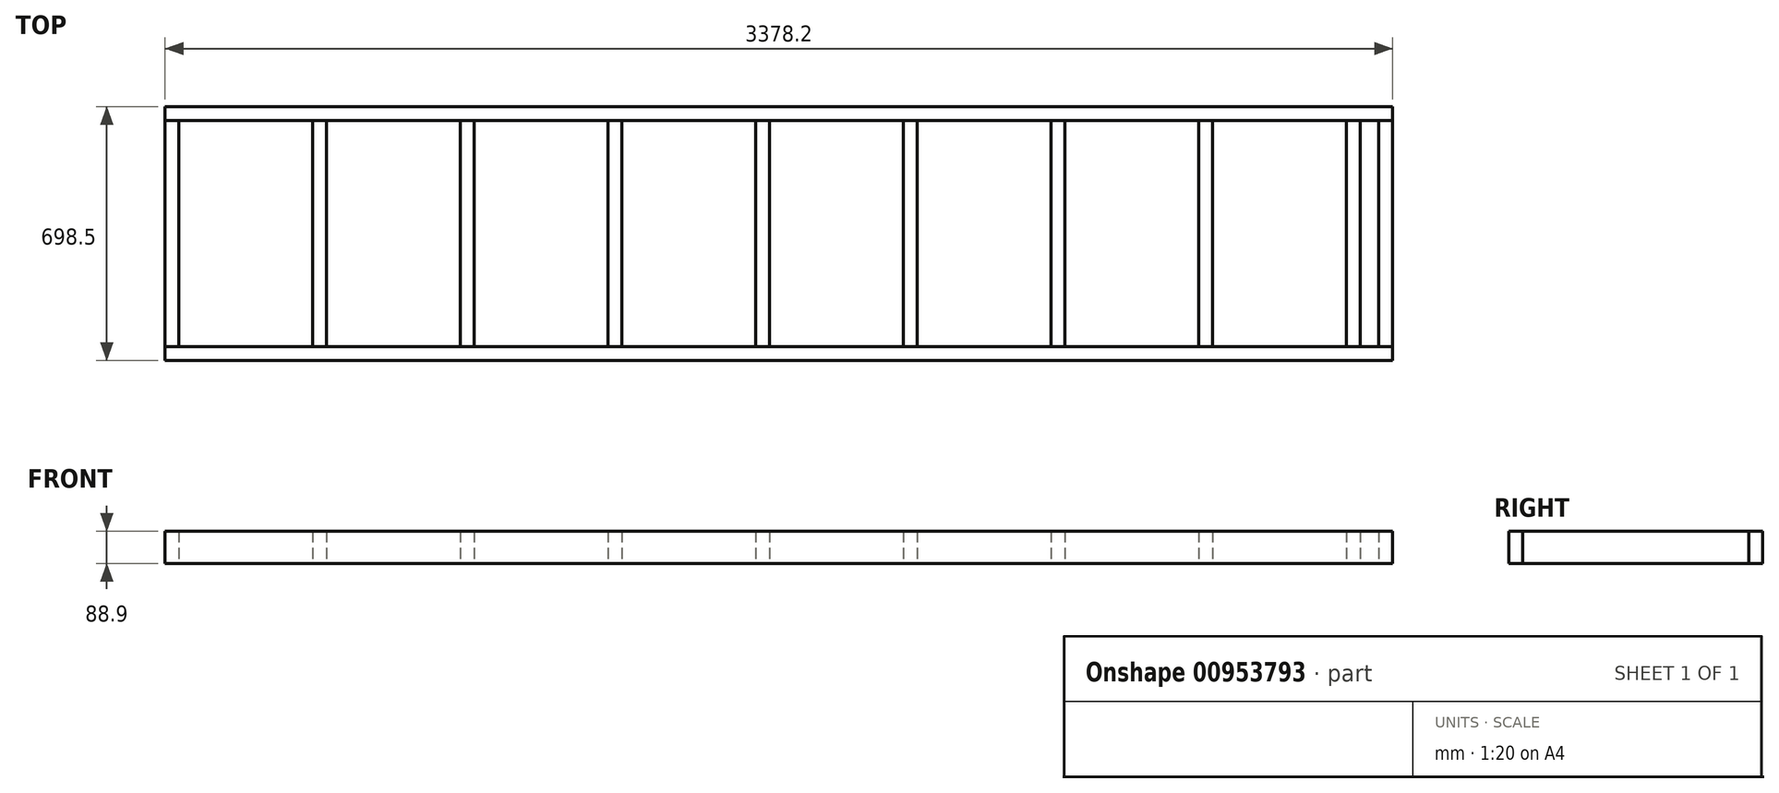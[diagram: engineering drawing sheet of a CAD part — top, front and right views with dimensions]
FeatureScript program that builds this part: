
annotation { "Feature Type Name" : "Feature", "Feature Type Description" : "" }
export const myFeature = defineFeature(function(context is Context, id is Id, definition is map)
    precondition{}
    {
        {
            var Q0;
            Q0=qCreatedBy(makeId("Top.planeOp"),FACE);
            var sketch = newSketch(context, id + "F0", { "sketchPlane" : qUnion([Q0])});
            skLineSegment(sketch, "E0.bottom", {"start": v(0, 0) * mm, "end": v(3378.2, 0) * mm});
            skLineSegment(sketch, "E0.top", {"start": v(0, 698.5) * mm, "end": v(3378.2, 698.5) * mm});
            skLineSegment(sketch, "E0.left", {"start": v(0, 0) * mm, "end": v(0, 698.5) * mm});
            skLineSegment(sketch, "E0.right", {"start": v(3378.2, 0) * mm, "end": v(3378.2, 698.5) * mm});
            skLineSegment(sketch, "E1.0", {"start": v(38.1, 38.1) * mm, "end": v(3340.1, 38.1) * mm});
            skLineSegment(sketch, "E1.1", {"start": v(38.1, 38.1) * mm, "end": v(38.1, 660.4) * mm});
            skLineSegment(sketch, "E1.2", {"start": v(38.1, 660.4) * mm, "end": v(3340.1, 660.4) * mm});
            skLineSegment(sketch, "E1.3", {"start": v(3340.1, 38.1) * mm, "end": v(3340.1, 660.4) * mm});
            skLineSegment(sketch, "E2", {"start": v(38.1, 660.4) * mm, "end": v(0, 660.4) * mm});
            skLineSegment(sketch, "E3", {"start": v(38.1, 38.1) * mm, "end": v(0, 38.1) * mm});
            skLineSegment(sketch, "E4", {"start": v(3340.1, 660.4) * mm, "end": v(3378.2, 660.4) * mm});
            skLineSegment(sketch, "E5", {"start": v(3340.1, 38.1) * mm, "end": v(3378.2, 38.1) * mm});
            skSolve(sketch);
        }
        {
            var Q0;
            {var subQ1=sQuery(id+"F0.wireOp",EDGE,"E0.top");Q0=makeQuery(id+"F0.imprint","IMPRINT",FACE,{"disambiguationData":[TD([[makeQuery(id+"F0.imprint","IMPRINT",EDGE,{"derivedFrom":subQ1}),-1.0]])]});}
            extrude(context, id + "F1", {"entities" : qUnion([Q0]), "depth" : 88.9 * mm, "offsetDistance" : 25.4 * mm});
        }
        {
            var Q0;
            {var subQ1=sQuery(id+"F0.wireOp",EDGE,"E0.bottom");Q0=makeQuery(id+"F0.imprint","IMPRINT",FACE,{"disambiguationData":[TD([[makeQuery(id+"F0.imprint","IMPRINT",EDGE,{"derivedFrom":subQ1}),1.0]])]});}
            extrude(context, id + "F2", {"entities" : qUnion([Q0]), "depth" : 88.9 * mm, "offsetDistance" : 25.4 * mm});
        }
        {
            var Q0;
            Q0=makeQuery(id+"F0.imprint","IMPRINT",FACE,{"disambiguationData":[TD([[makeQuery(id+"F0.imprint","IMPRINT",EDGE,{"derivedFrom":sQuery(id+"F0.wireOp",EDGE,"E1.1")}),1.0]])]});
            extrude(context, id + "F3", {"entities" : qUnion([Q0]), "depth" : 88.9 * mm, "offsetDistance" : 25.4 * mm});
        }
        {
            var Q0;
            Q0=makeQuery(id+"F3.opExtrude","SWEPT_BODY",BODY,{"disambiguationData":[OSD([sQuery(id+"F0.wireOp",EDGE,"E0.left"),sQuery(id+"F0.wireOp",EDGE,"E1.1"),sQuery(id+"F0.wireOp",EDGE,"E2"),sQuery(id+"F0.wireOp",EDGE,"E3")])]});
            var Q1;
            Q1=makeQuery(id+"F3.opExtrude","SWEPT_FACE",FACE,{"disambiguationData":[OSD([sQuery(id+"F0.wireOp",EDGE,"E1.1")])]});
            transform(context, id + "F4", {"entities" : qUnion([Q0]), "transformType" : TransformType.TRANSLATION_DISTANCE, "transformDirection" : qUnion([Q1]), "distance" : 406.4 * mm, "makeCopy" : true});
        }
        {
            var Q0;
            Q0=makeQuery(id+"F4.opPattern","COPY",BODY,{"derivedFrom":makeQuery(id+"F3.opExtrude","SWEPT_BODY",BODY,{"disambiguationData":[OSD([sQuery(id+"F0.wireOp",EDGE,"E0.left"),sQuery(id+"F0.wireOp",EDGE,"E1.1"),sQuery(id+"F0.wireOp",EDGE,"E2"),sQuery(id+"F0.wireOp",EDGE,"E3")])]}),"instanceName":"1"});
            var Q1;
            Q1=makeQuery(id+"F4.opPattern","COPY",FACE,{"derivedFrom":makeQuery(id+"F3.opExtrude","SWEPT_FACE",FACE,{"disambiguationData":[OSD([sQuery(id+"F0.wireOp",EDGE,"E1.1")])]}),"instanceName":"1"});
            transform(context, id + "F5", {"entities" : qUnion([Q0]), "transformType" : TransformType.TRANSLATION_DISTANCE, "transformDirection" : qUnion([Q1]), "distance" : 406.4 * mm, "makeCopy" : true});
        }
        {
            var Q0;
            Q0=makeQuery(id+"F5.opPattern","COPY",BODY,{"derivedFrom":makeQuery(id+"F4.opPattern","COPY",BODY,{"derivedFrom":makeQuery(id+"F3.opExtrude","SWEPT_BODY",BODY,{"disambiguationData":[OSD([sQuery(id+"F0.wireOp",EDGE,"E0.left"),sQuery(id+"F0.wireOp",EDGE,"E1.1"),sQuery(id+"F0.wireOp",EDGE,"E2"),sQuery(id+"F0.wireOp",EDGE,"E3")])]}),"instanceName":"1"}),"instanceName":"1"});
            var Q1;
            Q1=makeQuery(id+"F5.opPattern","COPY",FACE,{"derivedFrom":makeQuery(id+"F4.opPattern","COPY",FACE,{"derivedFrom":makeQuery(id+"F3.opExtrude","SWEPT_FACE",FACE,{"disambiguationData":[OSD([sQuery(id+"F0.wireOp",EDGE,"E1.1")])]}),"instanceName":"1"}),"instanceName":"1"});
            transform(context, id + "F6", {"entities" : qUnion([Q0]), "transformType" : TransformType.TRANSLATION_DISTANCE, "transformDirection" : qUnion([Q1]), "distance" : 406.4 * mm, "makeCopy" : true});
        }
        {
            var Q0;
            Q0=makeQuery(id+"F6.opPattern","COPY",BODY,{"derivedFrom":makeQuery(id+"F5.opPattern","COPY",BODY,{"derivedFrom":makeQuery(id+"F4.opPattern","COPY",BODY,{"derivedFrom":makeQuery(id+"F3.opExtrude","SWEPT_BODY",BODY,{"disambiguationData":[OSD([sQuery(id+"F0.wireOp",EDGE,"E0.left"),sQuery(id+"F0.wireOp",EDGE,"E1.1"),sQuery(id+"F0.wireOp",EDGE,"E2"),sQuery(id+"F0.wireOp",EDGE,"E3")])]}),"instanceName":"1"}),"instanceName":"1"}),"instanceName":"1"});
            var Q1;
            Q1=makeQuery(id+"F6.opPattern","COPY",FACE,{"derivedFrom":makeQuery(id+"F5.opPattern","COPY",FACE,{"derivedFrom":makeQuery(id+"F4.opPattern","COPY",FACE,{"derivedFrom":makeQuery(id+"F3.opExtrude","SWEPT_FACE",FACE,{"disambiguationData":[OSD([sQuery(id+"F0.wireOp",EDGE,"E1.1")])]}),"instanceName":"1"}),"instanceName":"1"}),"instanceName":"1"});
            transform(context, id + "F7", {"entities" : qUnion([Q0]), "transformType" : TransformType.TRANSLATION_DISTANCE, "transformDirection" : qUnion([Q1]), "distance" : 406.4 * mm, "makeCopy" : true});
        }
        {
            var Q0;
            Q0=makeQuery(id+"F7.opPattern","COPY",BODY,{"derivedFrom":makeQuery(id+"F6.opPattern","COPY",BODY,{"derivedFrom":makeQuery(id+"F5.opPattern","COPY",BODY,{"derivedFrom":makeQuery(id+"F4.opPattern","COPY",BODY,{"derivedFrom":makeQuery(id+"F3.opExtrude","SWEPT_BODY",BODY,{"disambiguationData":[OSD([sQuery(id+"F0.wireOp",EDGE,"E0.left"),sQuery(id+"F0.wireOp",EDGE,"E1.1"),sQuery(id+"F0.wireOp",EDGE,"E2"),sQuery(id+"F0.wireOp",EDGE,"E3")])]}),"instanceName":"1"}),"instanceName":"1"}),"instanceName":"1"}),"instanceName":"1"});
            var Q1;
            Q1=makeQuery(id+"F7.opPattern","COPY",FACE,{"derivedFrom":makeQuery(id+"F6.opPattern","COPY",FACE,{"derivedFrom":makeQuery(id+"F5.opPattern","COPY",FACE,{"derivedFrom":makeQuery(id+"F4.opPattern","COPY",FACE,{"derivedFrom":makeQuery(id+"F3.opExtrude","SWEPT_FACE",FACE,{"disambiguationData":[OSD([sQuery(id+"F0.wireOp",EDGE,"E1.1")])]}),"instanceName":"1"}),"instanceName":"1"}),"instanceName":"1"}),"instanceName":"1"});
            transform(context, id + "F8", {"entities" : qUnion([Q0]), "transformType" : TransformType.TRANSLATION_DISTANCE, "transformDirection" : qUnion([Q1]), "distance" : 406.4 * mm, "makeCopy" : true});
        }
        {
            var Q0;
            Q0=makeQuery(id+"F8.opPattern","COPY",BODY,{"derivedFrom":makeQuery(id+"F7.opPattern","COPY",BODY,{"derivedFrom":makeQuery(id+"F6.opPattern","COPY",BODY,{"derivedFrom":makeQuery(id+"F5.opPattern","COPY",BODY,{"derivedFrom":makeQuery(id+"F4.opPattern","COPY",BODY,{"derivedFrom":makeQuery(id+"F3.opExtrude","SWEPT_BODY",BODY,{"disambiguationData":[OSD([sQuery(id+"F0.wireOp",EDGE,"E0.left"),sQuery(id+"F0.wireOp",EDGE,"E1.1"),sQuery(id+"F0.wireOp",EDGE,"E2"),sQuery(id+"F0.wireOp",EDGE,"E3")])]}),"instanceName":"1"}),"instanceName":"1"}),"instanceName":"1"}),"instanceName":"1"}),"instanceName":"1"});
            var Q1;
            Q1=makeQuery(id+"F8.opPattern","COPY",FACE,{"derivedFrom":makeQuery(id+"F7.opPattern","COPY",FACE,{"derivedFrom":makeQuery(id+"F6.opPattern","COPY",FACE,{"derivedFrom":makeQuery(id+"F5.opPattern","COPY",FACE,{"derivedFrom":makeQuery(id+"F4.opPattern","COPY",FACE,{"derivedFrom":makeQuery(id+"F3.opExtrude","SWEPT_FACE",FACE,{"disambiguationData":[OSD([sQuery(id+"F0.wireOp",EDGE,"E1.1")])]}),"instanceName":"1"}),"instanceName":"1"}),"instanceName":"1"}),"instanceName":"1"}),"instanceName":"1"});
            transform(context, id + "F9", {"entities" : qUnion([Q0]), "transformType" : TransformType.TRANSLATION_DISTANCE, "transformDirection" : qUnion([Q1]), "distance" : 406.4 * mm, "makeCopy" : true});
        }
        {
            var Q0;
            Q0=makeQuery(id+"F9.opPattern","COPY",BODY,{"derivedFrom":makeQuery(id+"F8.opPattern","COPY",BODY,{"derivedFrom":makeQuery(id+"F7.opPattern","COPY",BODY,{"derivedFrom":makeQuery(id+"F6.opPattern","COPY",BODY,{"derivedFrom":makeQuery(id+"F5.opPattern","COPY",BODY,{"derivedFrom":makeQuery(id+"F4.opPattern","COPY",BODY,{"derivedFrom":makeQuery(id+"F3.opExtrude","SWEPT_BODY",BODY,{"disambiguationData":[OSD([sQuery(id+"F0.wireOp",EDGE,"E0.left"),sQuery(id+"F0.wireOp",EDGE,"E1.1"),sQuery(id+"F0.wireOp",EDGE,"E2"),sQuery(id+"F0.wireOp",EDGE,"E3")])]}),"instanceName":"1"}),"instanceName":"1"}),"instanceName":"1"}),"instanceName":"1"}),"instanceName":"1"}),"instanceName":"1"});
            var Q1;
            Q1=makeQuery(id+"F9.opPattern","COPY",FACE,{"derivedFrom":makeQuery(id+"F8.opPattern","COPY",FACE,{"derivedFrom":makeQuery(id+"F7.opPattern","COPY",FACE,{"derivedFrom":makeQuery(id+"F6.opPattern","COPY",FACE,{"derivedFrom":makeQuery(id+"F5.opPattern","COPY",FACE,{"derivedFrom":makeQuery(id+"F4.opPattern","COPY",FACE,{"derivedFrom":makeQuery(id+"F3.opExtrude","SWEPT_FACE",FACE,{"disambiguationData":[OSD([sQuery(id+"F0.wireOp",EDGE,"E1.1")])]}),"instanceName":"1"}),"instanceName":"1"}),"instanceName":"1"}),"instanceName":"1"}),"instanceName":"1"}),"instanceName":"1"});
            transform(context, id + "F10", {"entities" : qUnion([Q0]), "transformType" : TransformType.TRANSLATION_DISTANCE, "transformDirection" : qUnion([Q1]), "distance" : 406.4 * mm, "makeCopy" : true});
        }
        {
            var Q0;
            Q0=makeQuery(id+"F10.opPattern","COPY",BODY,{"derivedFrom":makeQuery(id+"F9.opPattern","COPY",BODY,{"derivedFrom":makeQuery(id+"F8.opPattern","COPY",BODY,{"derivedFrom":makeQuery(id+"F7.opPattern","COPY",BODY,{"derivedFrom":makeQuery(id+"F6.opPattern","COPY",BODY,{"derivedFrom":makeQuery(id+"F5.opPattern","COPY",BODY,{"derivedFrom":makeQuery(id+"F4.opPattern","COPY",BODY,{"derivedFrom":makeQuery(id+"F3.opExtrude","SWEPT_BODY",BODY,{"disambiguationData":[OSD([sQuery(id+"F0.wireOp",EDGE,"E0.left"),sQuery(id+"F0.wireOp",EDGE,"E1.1"),sQuery(id+"F0.wireOp",EDGE,"E2"),sQuery(id+"F0.wireOp",EDGE,"E3")])]}),"instanceName":"1"}),"instanceName":"1"}),"instanceName":"1"}),"instanceName":"1"}),"instanceName":"1"}),"instanceName":"1"}),"instanceName":"1"});
            var Q1;
            Q1=makeQuery(id+"F10.opPattern","COPY",FACE,{"derivedFrom":makeQuery(id+"F9.opPattern","COPY",FACE,{"derivedFrom":makeQuery(id+"F8.opPattern","COPY",FACE,{"derivedFrom":makeQuery(id+"F7.opPattern","COPY",FACE,{"derivedFrom":makeQuery(id+"F6.opPattern","COPY",FACE,{"derivedFrom":makeQuery(id+"F5.opPattern","COPY",FACE,{"derivedFrom":makeQuery(id+"F4.opPattern","COPY",FACE,{"derivedFrom":makeQuery(id+"F3.opExtrude","SWEPT_FACE",FACE,{"disambiguationData":[OSD([sQuery(id+"F0.wireOp",EDGE,"E1.1")])]}),"instanceName":"1"}),"instanceName":"1"}),"instanceName":"1"}),"instanceName":"1"}),"instanceName":"1"}),"instanceName":"1"}),"instanceName":"1"});
            transform(context, id + "F11", {"entities" : qUnion([Q0]), "transformType" : TransformType.TRANSLATION_DISTANCE, "transformDirection" : qUnion([Q1]), "distance" : 406.4 * mm, "makeCopy" : true});
        }
        {
            var Q0;
            Q0=makeQuery(id+"F3.opExtrude","SWEPT_BODY",BODY,{"disambiguationData":[OSD([sQuery(id+"F0.wireOp",EDGE,"E0.left"),sQuery(id+"F0.wireOp",EDGE,"E1.1"),sQuery(id+"F0.wireOp",EDGE,"E2"),sQuery(id+"F0.wireOp",EDGE,"E3")])]});
            var Q1;
            Q1=sQuery(id+"F0.wireOp",VERTEX,"E3.end");
            var Q2;
            Q2=sQuery(id+"F0.wireOp",VERTEX,"E1.0.end");
            transform(context, id + "F12", {"entities" : qUnion([Q0]), "transformType" : TransformType.TRANSLATION_ENTITY, "oppositeDirectionEntity" : false, "transformLine" : qUnion([Q1, Q2]), "makeCopy" : true});
        }
    });
